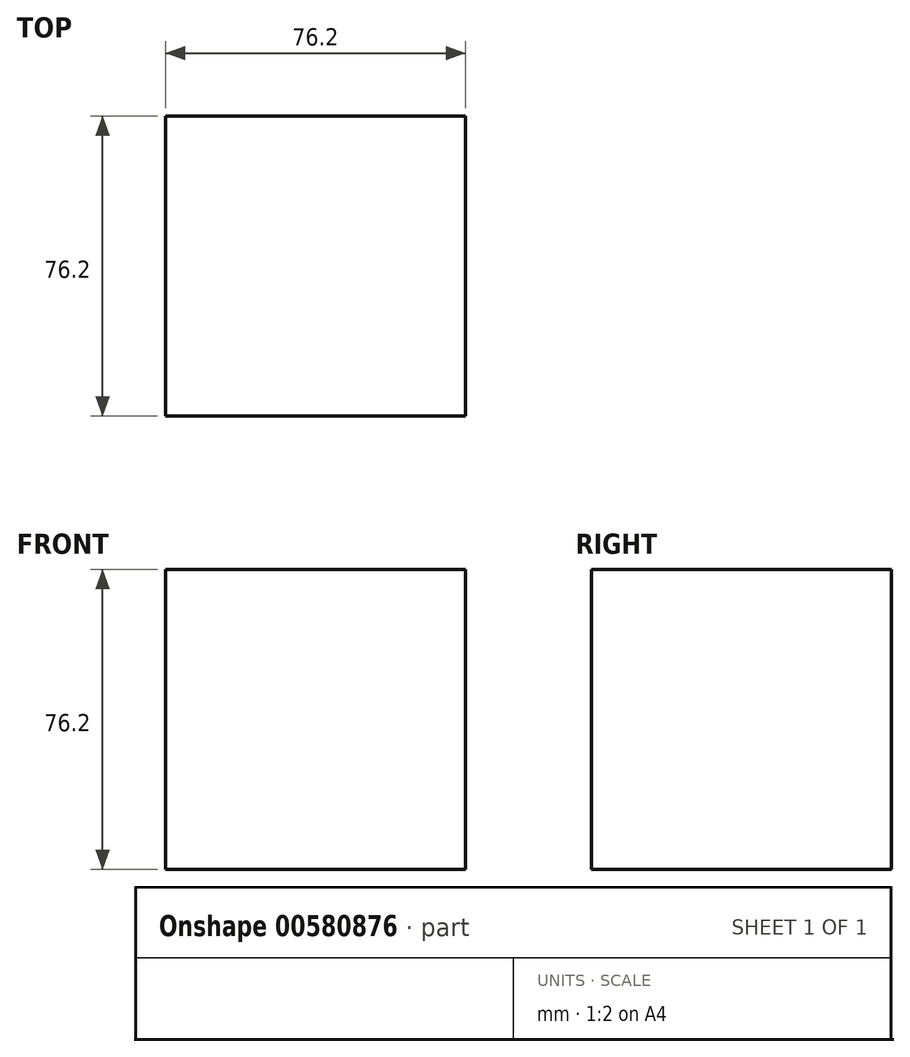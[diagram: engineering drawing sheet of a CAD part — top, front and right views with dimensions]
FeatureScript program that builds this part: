
annotation { "Feature Type Name" : "Feature", "Feature Type Description" : "" }
export const myFeature = defineFeature(function(context is Context, id is Id, definition is map)
    precondition{}
    {
        {
            var Q0;
            Q0=qCreatedBy(makeId("Front.planeOp"),FACE);
            var sketch = newSketch(context, id + "F0", { "sketchPlane" : qUnion([Q0])});
            skLineSegment(sketch, "E0.bottom", {"start": v(-38.23, 39.49) * mm, "end": v(37.97, 39.49) * mm});
            skLineSegment(sketch, "E0.top", {"start": v(-38.23, -36.71) * mm, "end": v(37.97, -36.71) * mm});
            skLineSegment(sketch, "E0.left", {"start": v(-38.23, 39.49) * mm, "end": v(-38.23, -36.71) * mm});
            skLineSegment(sketch, "E0.right", {"start": v(37.97, 39.49) * mm, "end": v(37.97, -36.71) * mm});
            skSolve(sketch);
        }
        {
            var Q0;
            Q0=makeQuery(id+"F0.imprint","IMPRINT",FACE,{"disambiguationData":[TD([[makeQuery(id+"F0.imprint","IMPRINT",EDGE,{"derivedFrom":sQuery(id+"F0.wireOp",EDGE,"E0.bottom")}),-1.0]])]});
            extrude(context, id + "F1", {"entities" : qUnion([Q0]), "depth" : 76.2 * mm, "offsetDistance" : 25.4 * mm});
        }
    });
